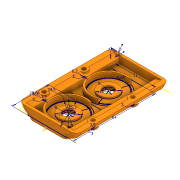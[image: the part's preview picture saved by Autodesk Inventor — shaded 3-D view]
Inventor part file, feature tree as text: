
AUTODESK INVENTOR PART (.ipt)
format: ipt  version: 2020.3 (Build 243373000, 373)  size: 329,216 bytes
history: native  units: mm
features: extrude x11, sketch x4, plane x1, mirror x1, fillet x1
ambient origin geometry x8: Origin, YZ Plane, XZ Plane, XY Plane, X Axis, Y Axis, Z Axis, Center Point
bodies: Solid1 (feature_tree)
feature tree (18):
  extrude  "Extrusion1"  Depth=72.2mm
  sketch  "Sketch2"  dims[d2=2.0mm d3=0.0mm d4=31.0mm]
  extrude  "Extrusion2"  Depth=31.0mm
  extrude  "Extrusion3"  Depth=24.5mm
  extrude  "Extrusion4"  Depth=3.95mm
  sketch  "Sketch4"  dims[d5=64.0mm d6=24.5mm]
  extrude  "Extrusion5"  Depth=3.95mm
  extrude  "Extrusion6"  Depth=3.95mm
  extrude  "Extrusion7"  Depth=3.95mm
  extrude  "Extrusion8"  Depth=3.95mm
  extrude  "Extrusion9"  Depth=3.95mm TaperAngle=0.0deg
  plane  "Work Plane1"
  mirror  "Mirror1"
  extrude  "Extrusion10"  Depth=3.95mm TaperAngle=0.0deg
  fillet  "Fillet1"  Radius=15.0mm
  extrude  "Extrusion11"  Depth=3.95mm
  sketch  "Sketch1"  dims[d0=45.0mm d1=72.2mm]
  sketch  "Sketch6"  dims[d7=28.66mm d8=4.34mm d9=25.5mm d10=28.0mm d12=15.0mm d13=8.0mm d14=4.0mm d15=0.0mm d16=1.0mm d17=0.0mm d18=15.0mm d19=8.0mm d21=1.0mm d22=0.0mm d24=3.0mm d25=3.0mm d26=3.0mm d27=3.0mm d28=3.5mm d29=3.5mm d30=10.0mm d31=7.5mm d32=4.0mm d33=74.75mm d34=0.0mm d35=10.0mm d36=0.0mm d37=8.0mm d38=16.5mm d39=0.0mm d40=6.2mm d41=6.2mm d42=6.0mm d43=0.0mm d44=1.0mm d45=0.0mm d46=-22.5mm d49=2.0mm d50=2.0mm d51=5.75mm d52=0.0mm d53=3.95mm d54=8.0mm d55=0.0mm d56=4.25mm d57=0.0mm]
